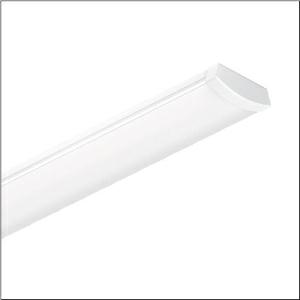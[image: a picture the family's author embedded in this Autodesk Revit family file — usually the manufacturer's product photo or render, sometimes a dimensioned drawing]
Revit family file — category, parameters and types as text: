
# Revit family: siluette_r__21_51ln12mkm40a_b89c
name_source: partatom
category: Lighting Fixtures
units: mm (PartAtom-declared; Revit-internal decimal feet)

## family parameters
Cut with Voids When Loaded = No
Host = Face
Light Source = No
Part Type = Normal
Room Calculation Point = No
Round Connector Dimension = Use Diameter
Shared = No

## types (1)
- --- (1 x LED, 2980 lm, 20.6 W, 5000K)
    Apparent Load = 21 VA
    CIE Flux Codes = 43 73 92 94 100
    Color Rendering = 80
    Color Temperature = 5000K
    Default Elevation = 1800 mm
    Description = Siluette® 21, office luminaire, primary optical cover: enclosure, of PC, frosted, light emission: direct distribution, primary light characteristic: symmetric, installation type: suspended mounting, surface-mounted, LED, rated luminous flux: 5.010lm, luminous efficacy: 135lm/W, light colour: 830/840/850, colour temperature: 3000/4000/5000K, with terminal, 3-pole, mains connection: 220..240V, AC, 50/60Hz, rated input power: 35W, housing, of sheet steel, white, length: 1.200mm, width: 152mm, height: 53mm, end cap, of PMMA, white, protection rating (complete): IP44, insulation class (complete): insulation class I (protective earthing), certification: CE, UKCA, protection symbol: D, permissible operating ambient temperature: -20..+40°C, contact your sales advisor before using the luminaires in applications with unclear chemical exposure, large temperature fluctuations or condensation-forming humidity, corresponds to IFS (International Featured Standards) requirements for safety and quality in the food industry, packaging unit: 1 piece
    Height = 52 mm  [stored 0.170604 ft]
    Lamp = 1 x LED
    Lamp Light Flux = 2980 lm
    Lamp Power = 20.6 W
    Lamp count = 1
    Length = 1185 mm
    Luminous efficacy = 145 lm/W
    Manufacturer = Siteco
    ModVariant = No
    Model = 51LN12MKM40A
    Mounting Place = Ceiling
    Mounting Type = Pendant
    Number of Poles = 1
    OnlyDefault = Yes
    Power Factor = 1
    Product Name = Siluette® 21
    Product group = office luminaire | ceiling pendant
    ProductGroupID = 902
    Protection Class = Protection class I
    Protection Degree = IP 44
    RLX_Detail_Level = 1
    RLX_Emergency_Light_Flux = 0 lm
    RLX_Emergency_Type = 0
    RLX_Emergency_Type_DB = No
    RlxData = <blob elided: 20225 chars, md5=2c6f4b02>
    Socket = socket
    Standby Power = 0 W
    System Light Flux = 2980 lm
    System Power = 21 W
    Type Comments = individual setting: colour temperature 5000K, luminous flux: 60 % | (OFF | OFF | ON) | 200 mA
    Type Image = l_1296910.jpg
    URL = http://relux.com
    VarID = @adj_019243
    Voltage = 0 V
    Weight = 0.00 kg
    Width = 152 mm

note: [stored X ft] marks values corroborated as IEEE doubles in the binary element streams (Revit-internal decimal feet)

## geometry (parser evidence)
native form markers: Blend x4, Sweep x13
no freeform markers — native parametric forms only
